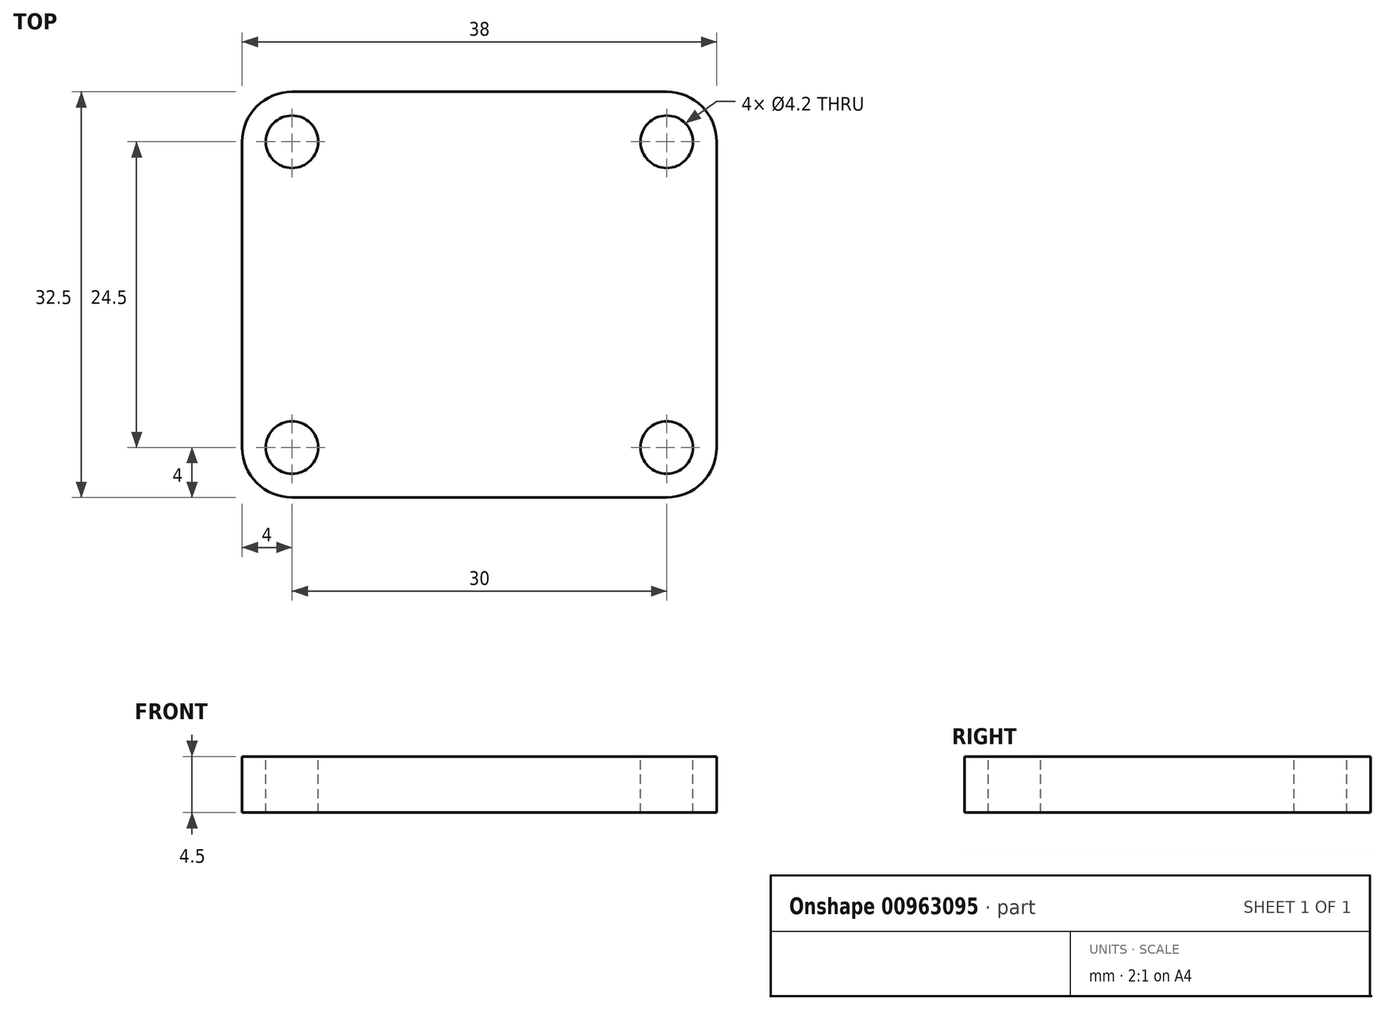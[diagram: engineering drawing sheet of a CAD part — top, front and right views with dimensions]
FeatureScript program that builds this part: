
annotation { "Feature Type Name" : "Feature", "Feature Type Description" : "" }
export const myFeature = defineFeature(function(context is Context, id is Id, definition is map)
    precondition{}
    {
        {
            var Q0;
            Q0=qCreatedBy(makeId("Top.planeOp"),FACE);
            var sketch = newSketch(context, id + "F0", { "sketchPlane" : qUnion([Q0])});
            skLineSegment(sketch, "E0.bottom", {"start": v(-15, 16.25) * mm, "end": v(15, 16.25) * mm});
            skLineSegment(sketch, "E0.top", {"start": v(-15, -16.25) * mm, "end": v(15, -16.25) * mm});
            skCircle(sketch, "E1", {"center": v(-15, 12.25) * mm, "radius": 2.1 * mm});
            skCircle(sketch, "E2", {"center": v(15, 12.25) * mm, "radius": 2.1 * mm});
            skCircle(sketch, "E3", {"center": v(-15, -12.25) * mm, "radius": 2.1 * mm});
            skCircle(sketch, "E4", {"center": v(15, -12.25) * mm, "radius": 2.1 * mm});
            skArc(sketch, "E5.filletArc", {"start": v(-15, 16.25) * mm, "mid": v(-17.83, 15.08) * mm, "end": v(-19, 12.25) * mm});
            skArc(sketch, "E6.filletArc", {"start": v(-19, -12.25) * mm, "mid": v(-17.83, -15.08) * mm, "end": v(-15, -16.25) * mm});
            skArc(sketch, "E7.filletArc", {"start": v(15, -16.25) * mm, "mid": v(17.83, -15.08) * mm, "end": v(19, -12.25) * mm});
            skArc(sketch, "E8.filletArc", {"start": v(19, 12.25) * mm, "mid": v(17.83, 15.08) * mm, "end": v(15, 16.25) * mm});
            skLineSegment(sketch, "E9", {"start": v(-19, 12.25) * mm, "end": v(-19, -12.25) * mm});
            skLineSegment(sketch, "E10", {"start": v(19, 12.25) * mm, "end": v(19, -12.25) * mm});
            skSolve(sketch);
        }
        {
            var Q0;
            Q0 = qSketchRegion(id + "F0", true);
            extrude(context, id + "F1", {"entities" : qUnion([Q0]), "oppositeDirection" : true, "depth" : 4.5 * mm, "offsetDistance" : 25 * mm});
        }
    });
